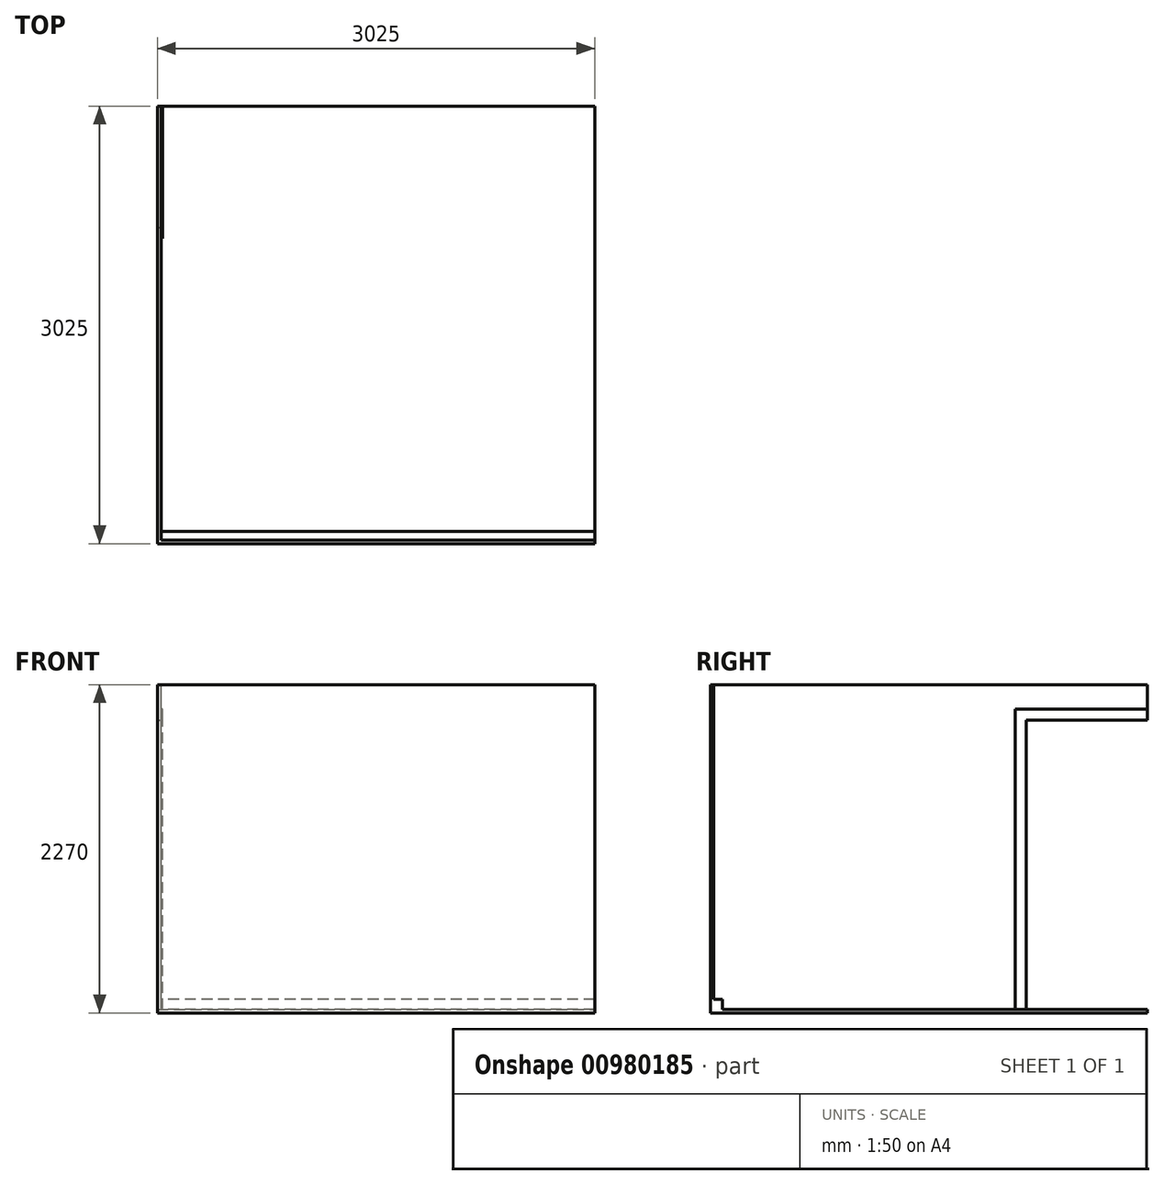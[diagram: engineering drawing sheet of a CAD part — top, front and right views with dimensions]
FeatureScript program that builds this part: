
annotation { "Feature Type Name" : "Feature", "Feature Type Description" : "" }
export const myFeature = defineFeature(function(context is Context, id is Id, definition is map)
    precondition{}
    {
        {
            var Q0;
            Q0=qCreatedBy(makeId("Top.planeOp"),FACE);
            var sketch = newSketch(context, id + "F0", { "sketchPlane" : qUnion([Q0])});
            skLineSegment(sketch, "E0.bottom", {"start": v(0, 0) * mm, "end": v(3000, 0) * mm});
            skLineSegment(sketch, "E0.top", {"start": v(0, 3000) * mm, "end": v(3000, 3000) * mm});
            skLineSegment(sketch, "E0.left", {"start": v(0, 0) * mm, "end": v(0, 3000) * mm});
            skLineSegment(sketch, "E0.right", {"start": v(3000, 0) * mm, "end": v(3000, 3000) * mm});
            skSolve(sketch);
        }
        {
            var Q0;
            Q0=makeQuery(id+"F0.imprint","IMPRINT",FACE,{"disambiguationData":[TD([[makeQuery(id+"F0.imprint","IMPRINT",EDGE,{"derivedFrom":sQuery(id+"F0.wireOp",EDGE,"E0.bottom")}),1.0]])]});
            extrude(context, id + "F1", {"entities" : qUnion([Q0]), "depth" : 25 * mm, "offsetDistance" : 25 * mm});
        }
        {
            var Q0;
            Q0=makeQuery(id+"F1.opExtrude","CAP_FACE",FACE,{"disambiguationData":[OSD([sQuery(id+"F0.wireOp",EDGE,"E0.bottom"),sQuery(id+"F0.wireOp",EDGE,"E0.top"),sQuery(id+"F0.wireOp",EDGE,"E0.left"),sQuery(id+"F0.wireOp",EDGE,"E0.right")])],"isStart":false});
            var sketch = newSketch(context, id + "F2", { "sketchPlane" : qUnion([Q0])});
            skLineSegment(sketch, "E1.bottom", {"start": v(3000, 0) * mm, "end": v(0, 0) * mm});
            skLineSegment(sketch, "E1.top", {"start": v(3000, 60) * mm, "end": v(0, 60) * mm});
            skLineSegment(sketch, "E1.left", {"start": v(3000, 0) * mm, "end": v(3000, 60) * mm});
            skLineSegment(sketch, "E1.right", {"start": v(0, 0) * mm, "end": v(0, 60) * mm});
            skSolve(sketch);
        }
        {
            var Q0;
            Q0=makeQuery(id+"F2.imprint","IMPRINT",FACE,{"disambiguationData":[TD([[makeQuery(id+"F2.imprint","IMPRINT",EDGE,{"derivedFrom":sQuery(id+"F2.wireOp",EDGE,"E1.bottom")}),1.0]])]});
            extrude(context, id + "F3", {"entities" : qUnion([Q0]), "operationType" : NewBodyOperationType.ADD, "depth" : 70 * mm, "offsetDistance" : 25 * mm});
        }
        {
            var Q0;
            Q0=makeQuery(id+"F3.boolean.opBoolean","MERGE",FACE,{"derivedFrom":[makeQuery(id+"F1.opExtrude","SWEPT_FACE",FACE,{"disambiguationData":[OSD([sQuery(id+"F0.wireOp",EDGE,"E0.bottom")])]}),makeQuery(id+"F3.opExtrude","SWEPT_FACE",FACE,{"disambiguationData":[OSD([sQuery(id+"F2.wireOp",EDGE,"E1.bottom")])]})]});
            var sketch = newSketch(context, id + "F4", { "sketchPlane" : qUnion([Q0])});
            skLineSegment(sketch, "E2.bottom", {"start": v(0, 0) * mm, "end": v(3000, 0) * mm});
            skLineSegment(sketch, "E2.top", {"start": v(0, 2270) * mm, "end": v(3000, 2270) * mm});
            skLineSegment(sketch, "E2.left", {"start": v(0, 0) * mm, "end": v(0, 2270) * mm});
            skLineSegment(sketch, "E2.right", {"start": v(3000, 0) * mm, "end": v(3000, 2270) * mm});
            skSolve(sketch);
        }
        {
            var Q0;
            {var subQ0=sQuery(id+"F4.wireOp",EDGE,"E2.top");Q0=makeQuery(id+"F4.imprint","IMPRINT",FACE,{"disambiguationData":[TD([[makeQuery(id+"F4.imprint","IMPRINT",EDGE,{"derivedFrom":subQ0}),-1.0]])]});}
            var Q1;
            {var subQ0=sQuery(id+"F4.wireOp",EDGE,"E2.bottom");Q1=makeQuery(id+"F4.imprint","IMPRINT",FACE,{"disambiguationData":[TD([[makeQuery(id+"F4.imprint","IMPRINT",EDGE,{"derivedFrom":subQ0}),1.0]])]});}
            extrude(context, id + "F5", {"entities" : qUnion([Q0, Q1]), "operationType" : NewBodyOperationType.ADD, "depth" : 25 * mm, "offsetDistance" : 25 * mm});
        }
        {
            var Q0;
            Q0=makeQuery(id+"F5.boolean.opBoolean","MERGE",FACE,{"derivedFrom":[makeQuery(id+"F3.boolean.opBoolean","MERGE",FACE,{"derivedFrom":[makeQuery(id+"F1.opExtrude","SWEPT_FACE",FACE,{"disambiguationData":[OSD([sQuery(id+"F0.wireOp",EDGE,"E0.left")])]}),makeQuery(id+"F3.opExtrude","SWEPT_FACE",FACE,{"disambiguationData":[OSD([sQuery(id+"F2.wireOp",EDGE,"E1.right")])]})]}),makeQuery(id+"F5.opExtrude","SWEPT_FACE",FACE,{"disambiguationData":[OSD([sQuery(id+"F4.wireOp",EDGE,"E2.left")])]})]});
            var sketch = newSketch(context, id + "F6", { "sketchPlane" : qUnion([Q0])});
            skLineSegment(sketch, "E3.bottom", {"start": v(25, 0) * mm, "end": v(-3000, 0) * mm});
            skLineSegment(sketch, "E3.top", {"start": v(25, 2270) * mm, "end": v(-3000, 2270) * mm});
            skLineSegment(sketch, "E3.left", {"start": v(25, 0) * mm, "end": v(25, 2270) * mm});
            skLineSegment(sketch, "E3.right", {"start": v(-3000, 0) * mm, "end": v(-3000, 2270) * mm});
            skSolve(sketch);
        }
        {
            var Q0;
            {var subQ0=sQuery(id+"F2.wireOp",EDGE,"E1.right");Q0=makeQuery(id+"F6.imprint","IMPRINT",FACE,{"disambiguationData":[TD([[makeQuery(id+"F6.imprint","IMPRINT",EDGE,{"derivedFrom":makeQuery(id+"F3.opExtrude","CAP_EDGE",EDGE,{"disambiguationData":[OSD([subQ0])],"isStart":false})}),-1.0]])]});}
            var Q1;
            {var subQ4=sQuery(id+"F6.wireOp",EDGE,"E3.bottom");Q1=makeQuery(id+"F6.imprint","IMPRINT",FACE,{"disambiguationData":[TD([[makeQuery(id+"F6.imprint","IMPRINT",EDGE,{"derivedFrom":subQ4}),-1.0]])]});}
            extrude(context, id + "F7", {"entities" : qUnion([Q0, Q1]), "operationType" : NewBodyOperationType.ADD, "depth" : 25 * mm, "offsetDistance" : 25 * mm});
        }
        {
            var Q0;
            Q0=makeQuery(id+"F7.opExtrude","CAP_FACE",FACE,{"disambiguationData":[OSD([sQuery(id+"F6.wireOp",EDGE,"E3.bottom"),sQuery(id+"F6.wireOp",EDGE,"E3.top"),sQuery(id+"F6.wireOp",EDGE,"E3.left"),sQuery(id+"F6.wireOp",EDGE,"E3.right")])],"isStart":true});
            var sketch = newSketch(context, id + "F8", { "sketchPlane" : qUnion([Q0])});
            skLineSegment(sketch, "E4.bottom", {"start": v(2160, 25) * mm, "end": v(3000, 25) * mm});
            skLineSegment(sketch, "E4.top", {"start": v(2160, 2025) * mm, "end": v(3000, 2025) * mm});
            skLineSegment(sketch, "E4.left", {"start": v(2160, 25) * mm, "end": v(2160, 2025) * mm});
            skLineSegment(sketch, "E4.right", {"start": v(3000, 25) * mm, "end": v(3000, 2025) * mm});
            skLineSegment(sketch, "E5.0", {"start": v(2085, 2100) * mm, "end": v(3000, 2100) * mm});
            skLineSegment(sketch, "E5.1", {"start": v(2085, 25) * mm, "end": v(2085, 2100) * mm});
            skSolve(sketch);
        }
        {
            var Q0;
            Q0=makeQuery(id+"F8.imprint","IMPRINT",FACE,{"disambiguationData":[TD([[makeQuery(id+"F8.imprint","IMPRINT",EDGE,{"derivedFrom":sQuery(id+"F8.wireOp",EDGE,"E4.bottom")}),1.0]])]});
            extrude(context, id + "F9", {"entities" : qUnion([Q0]), "operationType" : NewBodyOperationType.REMOVE, "oppositeDirection" : true, "depth" : 25 * mm, "offsetDistance" : 25 * mm});
        }
        {
            var Q0;
            {var subQ3=sQuery(id+"F8.wireOp",EDGE,"E4.top");Q0=makeQuery(id+"F8.imprint","IMPRINT",FACE,{"disambiguationData":[TD([[makeQuery(id+"F8.imprint","IMPRINT",EDGE,{"derivedFrom":subQ3}),1.0]])]});}
            extrude(context, id + "F10", {"entities" : qUnion([Q0]), "operationType" : NewBodyOperationType.ADD, "depth" : 10 * mm, "offsetDistance" : 25 * mm});
        }
    });
